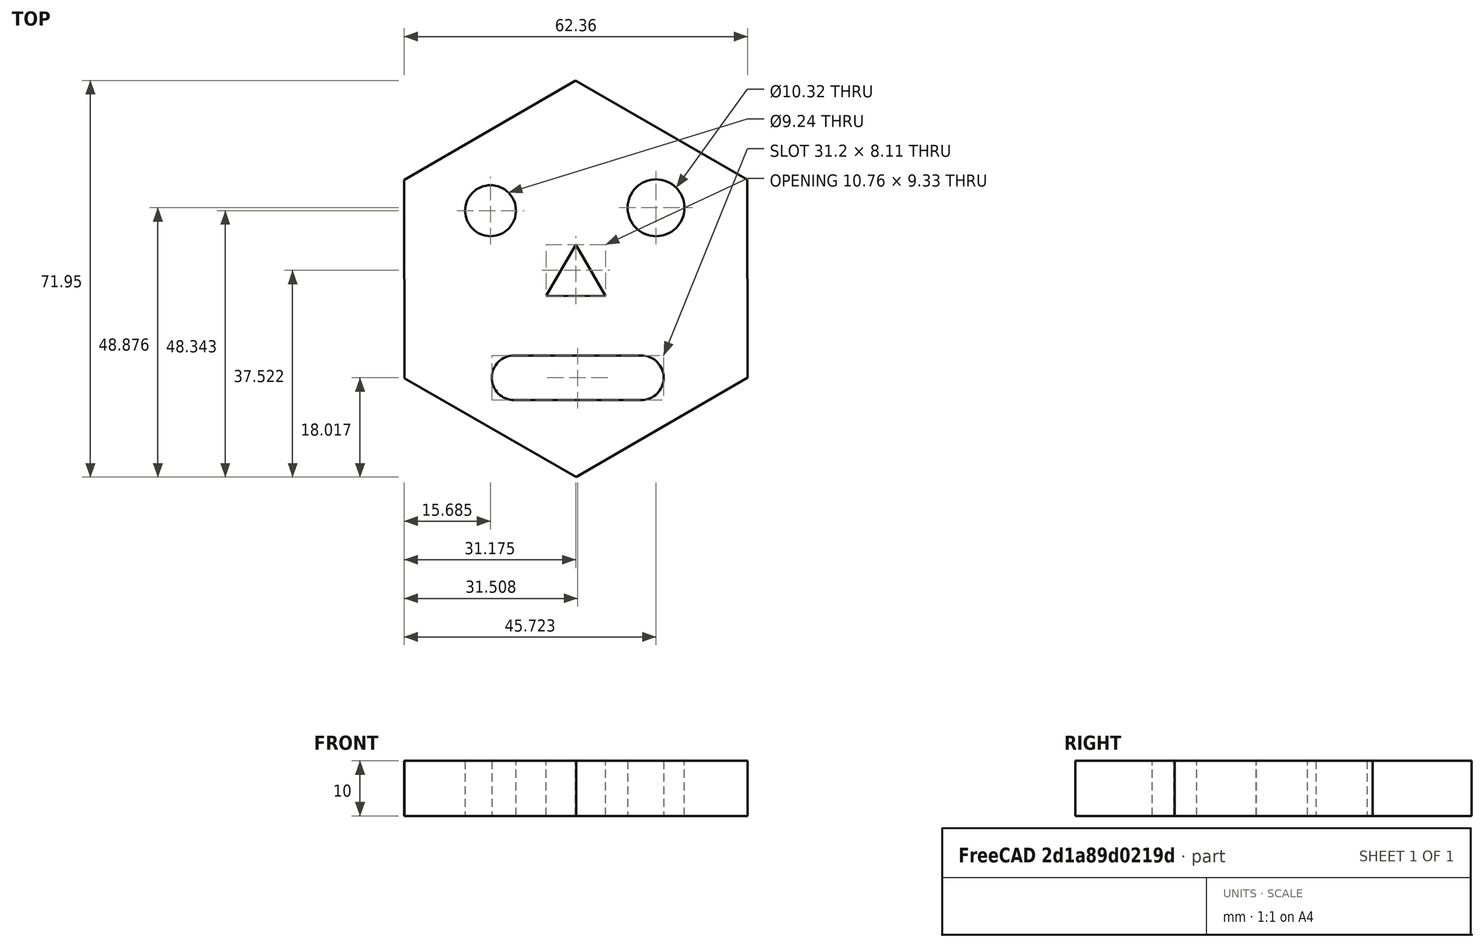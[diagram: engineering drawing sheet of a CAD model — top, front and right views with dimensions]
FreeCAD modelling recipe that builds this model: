
FCSTD DOCUMENT  (FreeCAD 1.0R38642 (Git))
Label: Opgave_1.0.2
License: All rights reserved
LicenseURL: http://en.wikipedia.org/wiki/All_rights_reserved
objects: Sketcher::SketchObject×1, PartDesign::Pad×1, PartDesign::Body×1
note: 6 computed .brp shape members not serialized (recipe doc carries the construction recipe); baked Part::Feature solids carry a one-line shape summary decoded from their .brp

FEATURE [Sketcher::SketchObject] Sketch
  ArcFitTolerance = 1e-06
  AttachmentSupport = -> [XY_Plane]
  FullyConstrained = false
  MakeInternals = false
  MapMode = 5
  sketch-geometry (17):
    g0: LineSegment StartX=96.7236 StartY=31.1383 StartZ=0 EndX=96.6741 EndY=67.1161 EndZ=0
    g1: LineSegment StartX=96.6741 StartY=67.1161 StartZ=0 EndX=65.4917 EndY=85.0621 EndZ=0
    g2: LineSegment StartX=65.4917 StartY=85.0621 StartZ=0 EndX=34.3588 EndY=67.0304 EndZ=0
    g3: LineSegment StartX=34.3588 StartY=67.0304 StartZ=0 EndX=34.4083 EndY=31.0527 EndZ=0
    g4: LineSegment StartX=34.4083 StartY=31.0527 StartZ=0 EndX=65.5907 EndY=13.1066 EndZ=0
    g5: LineSegment StartX=65.5907 StartY=13.1066 StartZ=0 EndX=96.7236 EndY=31.1383 EndZ=0
    g6: Circle [constr] CenterX=65.5412 CenterY=49.0844 CenterZ=0 NormalX=0 NormalY=0 NormalZ=1 AngleXU=0 Radius=35.9778
    g7: Circle CenterX=50.0453 CenterY=61.4527 CenterZ=0 NormalX=0 NormalY=0 NormalZ=1 AngleXU=0 Radius=4.61885
    g8: Circle CenterX=80.0827 CenterY=61.986 CenterZ=0 NormalX=0 NormalY=0 NormalZ=1 AngleXU=0 Radius=5.15796
    g9: ArcOfCircle CenterX=54.3254 CenterY=31.1269 CenterZ=0 NormalX=0 NormalY=0 NormalZ=1 AngleXU=0 Radius=4.05549 StartAngle=1.5708 EndAngle=4.71239
    g10: ArcOfCircle CenterX=77.4117 CenterY=31.1269 CenterZ=0 NormalX=0 NormalY=0 NormalZ=1 AngleXU=0 Radius=4.05549 StartAngle=4.71239 EndAngle=7.85398
    g11: LineSegment StartX=54.3254 StartY=35.1823 StartZ=0 EndX=77.4117 EndY=35.1823 EndZ=0
    g12: LineSegment StartX=54.3254 StartY=27.0714 StartZ=0 EndX=77.4117 EndY=27.0714 EndZ=0
    g13: LineSegment StartX=65.5538 StartY=55.2965 StartZ=0 EndX=60.155 EndY=45.9892 EndZ=0
    g14: LineSegment StartX=60.155 StartY=45.9892 StartZ=0 EndX=70.9148 EndY=45.9674 EndZ=0
    g15: LineSegment StartX=70.9148 StartY=45.9674 StartZ=0 EndX=65.5538 EndY=55.2965 EndZ=0
    g16: Circle [constr] CenterX=65.5412 CenterY=49.0844 CenterZ=0 NormalX=0 NormalY=0 NormalZ=1 AngleXU=0 Radius=6.21217
  constraints (28):
    c: Coincident(g0,g1)
    c: Coincident(g1,g2)
    c: Coincident(g2,g3)
    c: Coincident(g3,g4)
    c: Coincident(g4,g5)
    c: Coincident(g5,g0)
    c: Equal(g0, g1-g5) x5
    c: PointOnObject(g0,g6)
    c: PointOnObject(g1,g6)
    c: PointOnObject(g2,g6)
    c: PointOnObject(g3,g6)
    c: PointOnObject(g4,g6)
    c: PointOnObject(g5,g6)
    c: Tangent(g9,g11) = 1.5708
    c: Tangent(g9,g12) = -1.5708
    c: Tangent(g10,g11) = 1.5708
    c: Tangent(g10,g12) = -1.5708
    c: Equal(g9,g10)
    c: Horizontal(g12)
    c: Coincident(g13,g14)
    c: Coincident(g14,g15)
    c: Coincident(g15,g13)
    c: Equal(g13,g14)
    c: Equal(g13,g15)
    c: PointOnObject(g13,g16)
    c: PointOnObject(g14,g16)
    c: PointOnObject(g15,g16)
    c: Coincident(g6,g16)
FEATURE [PartDesign::Pad] Pad
  Direction = (0,0,1)
  Length = 10
  Length2 = 10
  Profile = -> Sketch
  ReferenceAxis = -> Sketch [N_Axis]
  Refine = true
  Suppressed = false
  Type = 0
FEATURE [PartDesign::Body] Body
  AllowCompound = true
  Group = -> [Sketch,Pad]
  Origin = -> Origin
  Tip = -> Pad
